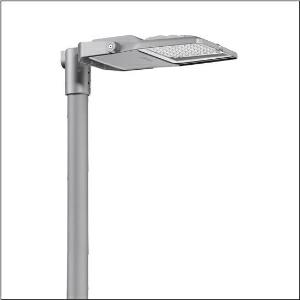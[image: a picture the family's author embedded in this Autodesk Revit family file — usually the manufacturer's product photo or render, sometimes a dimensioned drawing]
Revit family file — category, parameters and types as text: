
# Revit family: floodlight_fl_21_mini___pl64_5xa7775c2e3a_8880
name_source: partatom
category: Lighting Fixtures
units: mm (PartAtom-declared; Revit-internal decimal feet)

## family parameters
Cut with Voids When Loaded = No
Host = Face
Light Source = No
Part Type = Normal
Room Calculation Point = No
Round Connector Dimension = Use Diameter
Shared = No

## types (1)
- --- (1 x LED, 11770 lm, 89 W, 3000K)
    Apparent Load = 89 VA
    CIE Flux Codes = 28 80 98 100 100
    Color Rendering = 70
    Color Temperature = 3000K
    Default Elevation = 1800 mm
    Description = Floodlight FL 21 mini, floodlight, primary light control with lens, of PMMA, primary optical cover: protective disc, of toughened safety glass, transparent, light distribution: PL64, light emission: direct distribution, installation type: surface-mounted, LED, High Power LED, rated luminous flux: 11.770lm, luminous efficacy: 132lm/W, light colour: 730, colour temperature: 3000K, control: flexible luminous flux parameterisation, time-dependent luminous flux control, constant luminous flux control, overheat protection, presetting dimming logarithmic, with terminal, 6-pole, mains connection: 220..240V, AC, 50/60Hz, start of lifetime: 89W, end of service life: 94W, reduction: 43W, luminaire housing, of diecast aluminium, powder-coated, Siteco® metallic grey (DB 702S), corrosivity category C5 mid according to DIN EN ISO 12944, sealing non-destructively replaceable, please order mast flange separately, mast bracket, of steel, galvanised, powder-coated, Siteco® metallic grey (DB 702S), Smart Interface above, protection rating (complete): IP66, insulation class (complete): insulation class II (safety insulation), certification: CE, ENEC, VDE, protection symbol: D, impact resistance: IK08, permissible operating ambient temperature: -40..+40°C, permissible operating ambient temperature for outdoor applications: -40..+50°C, standard: DIN EN 12944, LABS conformity tested according to VDMA 24364:2018-05, packaging unit: 1 piece

Light Distribution: PL64
    Height = 70 mm
    Lamp = 1 x LED
    Lamp Light Flux = 11770 lm
    Lamp Power = 89 W
    Lamp count = 1
    Length = 485 mm
    Luminous efficacy = 132 lm/W
    Manufacturer = Siteco
    ModVariant = No
    Model = 5XA7775C2E3A
    Number of Poles = 1
    OnlyDefault = Yes
    Power Factor = 1
    Product Name = Floodlight FL 21 mini | PL64
    Product group = floodlight | pylon annexe
    ProductGroupID = 6200
    Protection Class = Protection class II
    Protection Degree = IP 66
    RLX_Detail_Level = 1
    RLX_Emergency_Light_Flux = 0 lm
    RLX_Emergency_Type = 0
    RLX_Emergency_Type_DB = No
    RlxData = <blob elided: 100849 chars, md5=2d37db5c>
    Socket = socket
    Standby Power = 0 W
    System Light Flux = 11770 lm
    System Power = 89 W
    Type Comments = factory setting: luminous flux: 100 % | dim-lin: 254 | 456 mA
    Type Image = l_1007125.jpg
    URL = http://relux.com
    VarID = @adj_097711
    Voltage = 0 V
    Weight = 0.00 kg
    Width = 337 mm

## geometry (parser evidence)
native form markers: Blend x4, Sweep x12
no freeform markers — native parametric forms only
